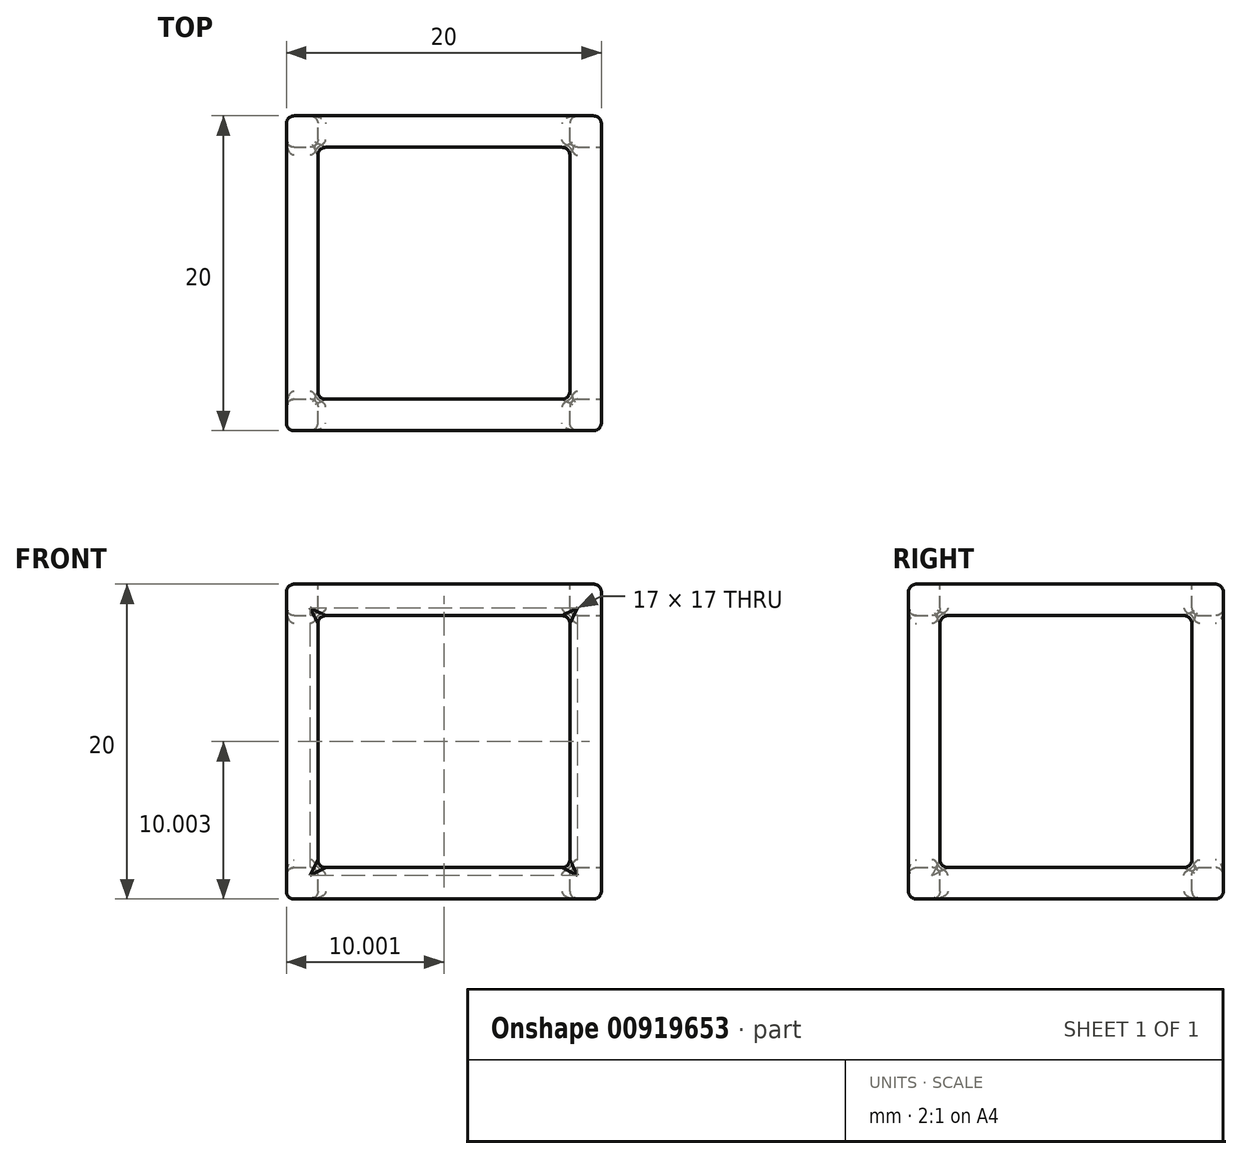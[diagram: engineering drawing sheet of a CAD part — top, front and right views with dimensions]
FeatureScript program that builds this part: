
annotation { "Feature Type Name" : "Feature", "Feature Type Description" : "" }
export const myFeature = defineFeature(function(context is Context, id is Id, definition is map)
    precondition{}
    {
        {
            var Q0;
            Q0=qCreatedBy(makeId("Front.planeOp"),FACE);
            var sketch = newSketch(context, id + "F0", { "sketchPlane" : qUnion([Q0])});
            skLineSegment(sketch, "E0.bottom", {"start": v(-48.8, 17.81) * mm, "end": v(-28.8, 17.81) * mm});
            skLineSegment(sketch, "E0.top", {"start": v(-48.8, -2.19) * mm, "end": v(-28.8, -2.19) * mm});
            skLineSegment(sketch, "E0.left", {"start": v(-48.8, 17.81) * mm, "end": v(-48.8, -2.19) * mm});
            skLineSegment(sketch, "E0.right", {"start": v(-28.8, 17.81) * mm, "end": v(-28.8, -2.23) * mm});
            skLineSegment(sketch, "E1.bottom", {"start": v(-46.8, 15.81) * mm, "end": v(-30.8, 15.81) * mm});
            skLineSegment(sketch, "E1.top", {"start": v(-46.8, -0.19) * mm, "end": v(-30.8, -0.19) * mm});
            skLineSegment(sketch, "E1.left", {"start": v(-46.8, 15.81) * mm, "end": v(-46.8, -0.19) * mm});
            skLineSegment(sketch, "E1.right", {"start": v(-30.8, 15.81) * mm, "end": v(-30.8, -0.19) * mm});
            skPoint(sketch, "E2.visualSharp", {"position": v(-46.8, 15.81) * mm});
            skPoint(sketch, "E3.visualSharp", {"position": v(-48.8, 17.81) * mm});
            skPoint(sketch, "E4.visualSharp", {"position": v(-30.8, 15.81) * mm});
            skPoint(sketch, "E5.visualSharp", {"position": v(-30.8, -0.19) * mm});
            skPoint(sketch, "E6.visualSharp", {"position": v(-46.8, -0.19) * mm});
            skPoint(sketch, "E7.visualSharp", {"position": v(-48.8, -2.19) * mm});
            skPoint(sketch, "E8.visualSharp", {"position": v(-28.8, -2.19) * mm});
            skPoint(sketch, "E9.visualSharp", {"position": v(-28.8, 17.81) * mm});
            skSolve(sketch);
        }
        {
            var Q0;
            Q0 = qSketchRegion(id + "F0", true);
            extrude(context, id + "F1", {"entities" : qUnion([Q0]), "depth" : 20 * mm, "offsetDistance" : 25 * mm});
        }
        {
            var Q0;
            Q0=makeQuery(id+"F1.opExtrude","SWEPT_FACE",FACE,{"disambiguationData":[OSD([sQuery(id+"F0.wireOp",EDGE,"E0.right")])]});
            var sketch = newSketch(context, id + "F2", { "sketchPlane" : qUnion([Q0])});
            skLineSegment(sketch, "E10.bottom", {"start": v(-2, 15.81) * mm, "end": v(-18, 15.81) * mm});
            skLineSegment(sketch, "E10.top", {"start": v(-18, -0.19) * mm, "end": v(-2, -0.19) * mm});
            skLineSegment(sketch, "E10.left", {"start": v(-18, 15.81) * mm, "end": v(-18, -0.19) * mm});
            skLineSegment(sketch, "E10.right", {"start": v(-2, 15.81) * mm, "end": v(-2, -0.19) * mm});
            skSolve(sketch);
        }
        {
            var Q0;
            Q0 = qSketchRegion(id + "F2", true);
            extrude(context, id + "F3", {"entities" : qUnion([Q0]), "operationType" : NewBodyOperationType.REMOVE, "oppositeDirection" : true, "depth" : 25 * mm, "offsetDistance" : 25 * mm});
        }
        {
            var Q0;
            Q0=makeQuery(id+"F1.opExtrude","SWEPT_FACE",FACE,{"disambiguationData":[OSD([sQuery(id+"F0.wireOp",EDGE,"E0.bottom")])]});
            var sketch = newSketch(context, id + "F4", { "sketchPlane" : qUnion([Q0])});
            skLineSegment(sketch, "E11.bottom", {"start": v(-30.8, -18) * mm, "end": v(-46.8, -18) * mm});
            skLineSegment(sketch, "E11.top", {"start": v(-30.8, -2) * mm, "end": v(-46.8, -2) * mm});
            skLineSegment(sketch, "E11.left", {"start": v(-30.8, -18) * mm, "end": v(-30.8, -2) * mm});
            skLineSegment(sketch, "E11.right", {"start": v(-46.8, -18) * mm, "end": v(-46.8, -2) * mm});
            skSolve(sketch);
        }
        {
            var Q0;
            Q0 = qSketchRegion(id + "F4", true);
            extrude(context, id + "F5", {"entities" : qUnion([Q0]), "operationType" : NewBodyOperationType.REMOVE, "oppositeDirection" : true, "depth" : 25 * mm, "offsetDistance" : 25 * mm});
        }
        {
            var Q0;
            Q0=makeQuery(id+"F1.opExtrude","CAP_EDGE",EDGE,{"disambiguationData":[OSD([sQuery(id+"F0.wireOp",EDGE,"E0.bottom")])],"isStart":false});
            var Q1;
            Q1=makeQuery(id+"F1.opExtrude","CAP_EDGE",EDGE,{"disambiguationData":[OSD([sQuery(id+"F0.wireOp",EDGE,"E1.bottom")])],"isStart":false});
            var Q2;
            Q2=makeQuery(id+"F3.boolean.opBoolean","COPY",EDGE,{"derivedFrom":makeQuery(id+"F3.opExtrude","CAP_EDGE",EDGE,{"disambiguationData":[OSD([sQuery(id+"F2.wireOp",EDGE,"E10.left")])],"isStart":true})});
            var Q3;
            Q3=makeQuery(id+"F1.opExtrude","CAP_FACE",FACE,{"disambiguationData":[OSD([sQuery(id+"F0.wireOp",EDGE,"E0.bottom"),sQuery(id+"F0.wireOp",EDGE,"E0.top"),sQuery(id+"F0.wireOp",EDGE,"E0.left"),sQuery(id+"F0.wireOp",EDGE,"E0.right"),sQuery(id+"F0.wireOp",EDGE,"E1.bottom"),sQuery(id+"F0.wireOp",EDGE,"E1.top"),sQuery(id+"F0.wireOp",EDGE,"E1.left"),sQuery(id+"F0.wireOp",EDGE,"E1.right")])],"isStart":false});
            var Q4;
            Q4=makeQuery(id+"F3.boolean.opBoolean","INTERSECT",EDGE,{"derivedFrom":[makeQuery(id+"F1.opExtrude","SWEPT_FACE",FACE,{"disambiguationData":[OSD([sQuery(id+"F0.wireOp",EDGE,"E1.right")])]}),makeQuery(id+"F3.opExtrude","SWEPT_FACE",FACE,{"disambiguationData":[OSD([sQuery(id+"F2.wireOp",EDGE,"E10.left")])]})]});
            var Q5;
            Q5=makeQuery(id+"F3.boolean.opBoolean","INTERSECT",EDGE,{"derivedFrom":[makeQuery(id+"F1.opExtrude","SWEPT_FACE",FACE,{"disambiguationData":[OSD([sQuery(id+"F0.wireOp",EDGE,"E0.left")])]}),makeQuery(id+"F3.opExtrude","SWEPT_FACE",FACE,{"disambiguationData":[OSD([sQuery(id+"F2.wireOp",EDGE,"E10.left")])]})]});
            var Q6;
            Q6=makeQuery(id+"F3.boolean.opBoolean","INTERSECT",EDGE,{"derivedFrom":[makeQuery(id+"F1.opExtrude","SWEPT_FACE",FACE,{"disambiguationData":[OSD([sQuery(id+"F0.wireOp",EDGE,"E0.left")])]}),makeQuery(id+"F3.opExtrude","SWEPT_FACE",FACE,{"disambiguationData":[OSD([sQuery(id+"F2.wireOp",EDGE,"E10.bottom")])]})]});
            var Q7;
            Q7=makeQuery(id+"F5.boolean.opBoolean","INTERSECT",EDGE,{"derivedFrom":[makeQuery(id+"F3.boolean.opBoolean","MERGE",FACE,{"derivedFrom":[makeQuery(id+"F1.opExtrude","SWEPT_FACE",FACE,{"disambiguationData":[OSD([sQuery(id+"F0.wireOp",EDGE,"E1.bottom")])]})],"fromTools":[makeQuery(id+"F3.opExtrude","SWEPT_FACE",FACE,{"disambiguationData":[OSD([sQuery(id+"F2.wireOp",EDGE,"E10.bottom")])]})]}),makeQuery(id+"F5.opExtrude","SWEPT_FACE",FACE,{"disambiguationData":[OSD([sQuery(id+"F4.wireOp",EDGE,"E11.right")])]})]});
            var Q8;
            Q8=makeQuery(id+"F5.boolean.opBoolean","COPY",EDGE,{"derivedFrom":makeQuery(id+"F5.opExtrude","CAP_EDGE",EDGE,{"disambiguationData":[OSD([sQuery(id+"F4.wireOp",EDGE,"E11.right")])],"isStart":true})});
            var Q9;
            Q9=makeQuery(id+"F1.opExtrude","SWEPT_EDGE",EDGE,{"disambiguationData":[OSD([sQuery(id+"F0.wireOp",EDGE,"E0.bottom"),sQuery(id+"F0.wireOp",EDGE,"E0.left")])]});
            var Q10;
            Q10=makeQuery(id+"F3.boolean.opBoolean","INTERSECT",EDGE,{"derivedFrom":[makeQuery(id+"F1.opExtrude","SWEPT_FACE",FACE,{"disambiguationData":[OSD([sQuery(id+"F0.wireOp",EDGE,"E0.left")])]}),makeQuery(id+"F3.opExtrude","SWEPT_FACE",FACE,{"disambiguationData":[OSD([sQuery(id+"F2.wireOp",EDGE,"E10.top")])]})]});
            var Q11;
            Q11=makeQuery(id+"F5.boolean.opBoolean","INTERSECT",EDGE,{"derivedFrom":[makeQuery(id+"F3.boolean.opBoolean","MERGE",FACE,{"derivedFrom":[makeQuery(id+"F1.opExtrude","SWEPT_FACE",FACE,{"disambiguationData":[OSD([sQuery(id+"F0.wireOp",EDGE,"E1.top")])]})],"fromTools":[makeQuery(id+"F3.opExtrude","SWEPT_FACE",FACE,{"disambiguationData":[OSD([sQuery(id+"F2.wireOp",EDGE,"E10.top")])]})]}),makeQuery(id+"F5.opExtrude","SWEPT_FACE",FACE,{"disambiguationData":[OSD([sQuery(id+"F4.wireOp",EDGE,"E11.right")])]})]});
            var Q12;
            Q12=makeQuery(id+"F1.opExtrude","SWEPT_EDGE",EDGE,{"disambiguationData":[OSD([sQuery(id+"F0.wireOp",EDGE,"E0.top"),sQuery(id+"F0.wireOp",EDGE,"E0.left")])]});
            var Q13;
            Q13=makeQuery(id+"F1.opExtrude","CAP_EDGE",EDGE,{"disambiguationData":[OSD([sQuery(id+"F0.wireOp",EDGE,"E0.left")])],"isStart":true});
            var Q14;
            Q14=makeQuery(id+"F3.boolean.opBoolean","INTERSECT",EDGE,{"derivedFrom":[makeQuery(id+"F1.opExtrude","SWEPT_FACE",FACE,{"disambiguationData":[OSD([sQuery(id+"F0.wireOp",EDGE,"E0.left")])]}),makeQuery(id+"F3.opExtrude","SWEPT_FACE",FACE,{"disambiguationData":[OSD([sQuery(id+"F2.wireOp",EDGE,"E10.right")])]})]});
            fillet(context, id + "F6", {"entities" : qUnion([Q0, Q1, Q2, Q3, Q4, Q5, Q6, Q7, Q8, Q9, Q10, Q11, Q12, Q13, Q14]), "radius" : 0.5 * mm, "tangentPropagation" : true, "allowEdgeOverflow" : false});
        }
        {
            var Q0;
            Q0=makeQuery(id+"F5.boolean.opBoolean","INTERSECT",EDGE,{"derivedFrom":[makeQuery(id+"F1.opExtrude","SWEPT_FACE",FACE,{"disambiguationData":[OSD([sQuery(id+"F0.wireOp",EDGE,"E0.top")])]}),makeQuery(id+"F5.opExtrude","SWEPT_FACE",FACE,{"disambiguationData":[OSD([sQuery(id+"F4.wireOp",EDGE,"E11.bottom")])]})]});
            var Q1;
            Q1=makeQuery(id+"F1.opExtrude","SWEPT_EDGE",EDGE,{"disambiguationData":[OSD([sQuery(id+"F0.wireOp",EDGE,"E0.top"),sQuery(id+"F0.wireOp",EDGE,"E0.right")])]});
            var Q2;
            Q2=makeQuery(id+"F5.boolean.opBoolean","INTERSECT",EDGE,{"derivedFrom":[makeQuery(id+"F1.opExtrude","SWEPT_FACE",FACE,{"disambiguationData":[OSD([sQuery(id+"F0.wireOp",EDGE,"E0.top")])]}),makeQuery(id+"F5.opExtrude","SWEPT_FACE",FACE,{"disambiguationData":[OSD([sQuery(id+"F4.wireOp",EDGE,"E11.left")])]})]});
            var Q3;
            Q3=makeQuery(id+"F3.boolean.opBoolean","COPY",EDGE,{"derivedFrom":makeQuery(id+"F3.opExtrude","CAP_EDGE",EDGE,{"disambiguationData":[OSD([sQuery(id+"F2.wireOp",EDGE,"E10.top")])],"isStart":true})});
            var Q4;
            Q4=makeQuery(id+"F5.boolean.opBoolean","INTERSECT",EDGE,{"derivedFrom":[makeQuery(id+"F1.opExtrude","SWEPT_FACE",FACE,{"disambiguationData":[OSD([sQuery(id+"F0.wireOp",EDGE,"E0.top")])]}),makeQuery(id+"F5.opExtrude","SWEPT_FACE",FACE,{"disambiguationData":[OSD([sQuery(id+"F4.wireOp",EDGE,"E11.right")])]})]});
            var Q5;
            Q5=makeQuery(id+"F3.boolean.opBoolean","INTERSECT",EDGE,{"derivedFrom":[makeQuery(id+"F1.opExtrude","SWEPT_FACE",FACE,{"disambiguationData":[OSD([sQuery(id+"F0.wireOp",EDGE,"E1.left")])]}),makeQuery(id+"F3.opExtrude","SWEPT_FACE",FACE,{"disambiguationData":[OSD([sQuery(id+"F2.wireOp",EDGE,"E10.left")])]})]});
            var Q6;
            Q6=makeQuery(id+"F5.boolean.opBoolean","COPY",EDGE,{"derivedFrom":makeQuery(id+"F5.opExtrude","CAP_EDGE",EDGE,{"disambiguationData":[OSD([sQuery(id+"F4.wireOp",EDGE,"E11.bottom")])],"isStart":true})});
            var Q7;
            Q7=makeQuery(id+"F5.boolean.opBoolean","INTERSECT",EDGE,{"derivedFrom":[makeQuery(id+"F3.boolean.opBoolean","MERGE",FACE,{"derivedFrom":[makeQuery(id+"F1.opExtrude","SWEPT_FACE",FACE,{"disambiguationData":[OSD([sQuery(id+"F0.wireOp",EDGE,"E1.bottom")])]})],"fromTools":[makeQuery(id+"F3.opExtrude","SWEPT_FACE",FACE,{"disambiguationData":[OSD([sQuery(id+"F2.wireOp",EDGE,"E10.bottom")])]})]}),makeQuery(id+"F5.opExtrude","SWEPT_FACE",FACE,{"disambiguationData":[OSD([sQuery(id+"F4.wireOp",EDGE,"E11.bottom")])]})]});
            var Q8;
            Q8=makeQuery(id+"F1.opExtrude","SWEPT_EDGE",EDGE,{"disambiguationData":[OSD([sQuery(id+"F0.wireOp",EDGE,"E0.bottom"),sQuery(id+"F0.wireOp",EDGE,"E0.right")])]});
            var Q9;
            Q9=makeQuery(id+"F5.boolean.opBoolean","COPY",EDGE,{"derivedFrom":makeQuery(id+"F5.opExtrude","CAP_EDGE",EDGE,{"disambiguationData":[OSD([sQuery(id+"F4.wireOp",EDGE,"E11.left")])],"isStart":true})});
            var Q10;
            Q10=makeQuery(id+"F3.boolean.opBoolean","COPY",EDGE,{"derivedFrom":makeQuery(id+"F3.opExtrude","CAP_EDGE",EDGE,{"disambiguationData":[OSD([sQuery(id+"F2.wireOp",EDGE,"E10.bottom")])],"isStart":true})});
            var Q11;
            Q11=makeQuery(id+"F3.boolean.opBoolean","COPY",EDGE,{"derivedFrom":makeQuery(id+"F3.opExtrude","CAP_EDGE",EDGE,{"disambiguationData":[OSD([sQuery(id+"F2.wireOp",EDGE,"E10.right")])],"isStart":true})});
            var Q12;
            Q12=makeQuery(id+"F1.opExtrude","CAP_EDGE",EDGE,{"disambiguationData":[OSD([sQuery(id+"F0.wireOp",EDGE,"E0.right")])],"isStart":true});
            var Q13;
            Q13=makeQuery(id+"F1.opExtrude","CAP_EDGE",EDGE,{"disambiguationData":[OSD([sQuery(id+"F0.wireOp",EDGE,"E0.bottom")])],"isStart":true});
            var Q14;
            Q14=makeQuery(id+"F5.boolean.opBoolean","COPY",EDGE,{"derivedFrom":makeQuery(id+"F5.opExtrude","CAP_EDGE",EDGE,{"disambiguationData":[OSD([sQuery(id+"F4.wireOp",EDGE,"E11.top")])],"isStart":true})});
            var Q15;
            Q15=makeQuery(id+"F5.boolean.opBoolean","INTERSECT",EDGE,{"derivedFrom":[makeQuery(id+"F3.boolean.opBoolean","MERGE",FACE,{"derivedFrom":[makeQuery(id+"F1.opExtrude","SWEPT_FACE",FACE,{"disambiguationData":[OSD([sQuery(id+"F0.wireOp",EDGE,"E1.top")])]})],"fromTools":[makeQuery(id+"F3.opExtrude","SWEPT_FACE",FACE,{"disambiguationData":[OSD([sQuery(id+"F2.wireOp",EDGE,"E10.top")])]})]}),makeQuery(id+"F5.opExtrude","SWEPT_FACE",FACE,{"disambiguationData":[OSD([sQuery(id+"F4.wireOp",EDGE,"E11.bottom")])]})]});
            fillet(context, id + "F7", {"entities" : qUnion([Q0, Q1, Q2, Q3, Q4, Q5, Q6, Q7, Q8, Q9, Q10, Q11, Q12, Q13, Q14, Q15]), "radius" : 0.5 * mm, "tangentPropagation" : true, "allowEdgeOverflow" : false});
        }
        {
            var Q0;
            Q0=makeQuery(id+"F3.boolean.opBoolean","INTERSECT",EDGE,{"derivedFrom":[makeQuery(id+"F1.opExtrude","SWEPT_FACE",FACE,{"disambiguationData":[OSD([sQuery(id+"F0.wireOp",EDGE,"E1.left")])]}),makeQuery(id+"F3.opExtrude","SWEPT_FACE",FACE,{"disambiguationData":[OSD([sQuery(id+"F2.wireOp",EDGE,"E10.right")])]})]});
            var Q1;
            Q1=makeQuery(id+"F5.boolean.opBoolean","INTERSECT",EDGE,{"derivedFrom":[makeQuery(id+"F3.boolean.opBoolean","MERGE",FACE,{"derivedFrom":[makeQuery(id+"F1.opExtrude","SWEPT_FACE",FACE,{"disambiguationData":[OSD([sQuery(id+"F0.wireOp",EDGE,"E1.top")])]})],"fromTools":[makeQuery(id+"F3.opExtrude","SWEPT_FACE",FACE,{"disambiguationData":[OSD([sQuery(id+"F2.wireOp",EDGE,"E10.top")])]})]}),makeQuery(id+"F5.opExtrude","SWEPT_FACE",FACE,{"disambiguationData":[OSD([sQuery(id+"F4.wireOp",EDGE,"E11.top")])]})]});
            var Q2;
            Q2=makeQuery(id+"F5.boolean.opBoolean","INTERSECT",EDGE,{"derivedFrom":[makeQuery(id+"F1.opExtrude","SWEPT_FACE",FACE,{"disambiguationData":[OSD([sQuery(id+"F0.wireOp",EDGE,"E0.top")])]}),makeQuery(id+"F5.opExtrude","SWEPT_FACE",FACE,{"disambiguationData":[OSD([sQuery(id+"F4.wireOp",EDGE,"E11.top")])]})]});
            var Q3;
            Q3=makeQuery(id+"F1.opExtrude","CAP_EDGE",EDGE,{"disambiguationData":[OSD([sQuery(id+"F0.wireOp",EDGE,"E1.top")])],"isStart":true});
            var Q4;
            Q4=makeQuery(id+"F1.opExtrude","CAP_EDGE",EDGE,{"disambiguationData":[OSD([sQuery(id+"F0.wireOp",EDGE,"E1.left")])],"isStart":true});
            fillet(context, id + "F8", {"entities" : qUnion([Q0, Q1, Q2, Q3, Q4]), "radius" : 0.5 * mm, "tangentPropagation" : true, "allowEdgeOverflow" : false});
        }
        {
            var Q0;
            Q0=makeQuery(id+"F3.boolean.opBoolean","INTERSECT",EDGE,{"derivedFrom":[makeQuery(id+"F1.opExtrude","SWEPT_FACE",FACE,{"disambiguationData":[OSD([sQuery(id+"F0.wireOp",EDGE,"E1.right")])]}),makeQuery(id+"F3.opExtrude","SWEPT_FACE",FACE,{"disambiguationData":[OSD([sQuery(id+"F2.wireOp",EDGE,"E10.right")])]})]});
            var Q1;
            Q1=makeQuery(id+"F1.opExtrude","CAP_EDGE",EDGE,{"disambiguationData":[OSD([sQuery(id+"F0.wireOp",EDGE,"E1.right")])],"isStart":true});
            var Q2;
            Q2=makeQuery(id+"F5.boolean.opBoolean","INTERSECT",EDGE,{"derivedFrom":[makeQuery(id+"F3.boolean.opBoolean","MERGE",FACE,{"derivedFrom":[makeQuery(id+"F1.opExtrude","SWEPT_FACE",FACE,{"disambiguationData":[OSD([sQuery(id+"F0.wireOp",EDGE,"E1.top")])]})],"fromTools":[makeQuery(id+"F3.opExtrude","SWEPT_FACE",FACE,{"disambiguationData":[OSD([sQuery(id+"F2.wireOp",EDGE,"E10.top")])]})]}),makeQuery(id+"F5.opExtrude","SWEPT_FACE",FACE,{"disambiguationData":[OSD([sQuery(id+"F4.wireOp",EDGE,"E11.left")])]})]});
            fillet(context, id + "F9", {"entities" : qUnion([Q0, Q1, Q2]), "radius" : 0.5 * mm, "tangentPropagation" : true, "allowEdgeOverflow" : false});
        }
        {
            var Q0;
            Q0=makeQuery(id+"F1.opExtrude","CAP_EDGE",EDGE,{"disambiguationData":[OSD([sQuery(id+"F0.wireOp",EDGE,"E0.top")])],"isStart":true});
            var Q1;
            Q1=makeQuery(id+"F5.boolean.opBoolean","INTERSECT",EDGE,{"derivedFrom":[makeQuery(id+"F3.boolean.opBoolean","MERGE",FACE,{"derivedFrom":[makeQuery(id+"F1.opExtrude","SWEPT_FACE",FACE,{"disambiguationData":[OSD([sQuery(id+"F0.wireOp",EDGE,"E1.bottom")])]})],"fromTools":[makeQuery(id+"F3.opExtrude","SWEPT_FACE",FACE,{"disambiguationData":[OSD([sQuery(id+"F2.wireOp",EDGE,"E10.bottom")])]})]}),makeQuery(id+"F5.opExtrude","SWEPT_FACE",FACE,{"disambiguationData":[OSD([sQuery(id+"F4.wireOp",EDGE,"E11.top")])]})]});
            var Q2;
            Q2=makeQuery(id+"F1.opExtrude","CAP_EDGE",EDGE,{"disambiguationData":[OSD([sQuery(id+"F0.wireOp",EDGE,"E1.bottom")])],"isStart":true});
            var Q3;
            Q3=makeQuery(id+"F5.boolean.opBoolean","INTERSECT",EDGE,{"derivedFrom":[makeQuery(id+"F3.boolean.opBoolean","MERGE",FACE,{"derivedFrom":[makeQuery(id+"F1.opExtrude","SWEPT_FACE",FACE,{"disambiguationData":[OSD([sQuery(id+"F0.wireOp",EDGE,"E1.bottom")])]})],"fromTools":[makeQuery(id+"F3.opExtrude","SWEPT_FACE",FACE,{"disambiguationData":[OSD([sQuery(id+"F2.wireOp",EDGE,"E10.bottom")])]})]}),makeQuery(id+"F5.opExtrude","SWEPT_FACE",FACE,{"disambiguationData":[OSD([sQuery(id+"F4.wireOp",EDGE,"E11.left")])]})]});
            var Q4;
            {var subQ0=sQuery(id+"F0.wireOp",EDGE,"E1.left");var subQ1=sQuery(id+"F0.wireOp",EDGE,"E1.bottom");Q4=makeQuery(id+"F3.boolean.opBoolean","SPLIT",EDGE,{"disambiguationData":[TD([makeQuery(id+"F3.opExtrude","SWEPT_FACE",FACE,{"disambiguationData":[OSD([sQuery(id+"F2.wireOp",EDGE,"E10.left")])]})])],"derivedFrom":makeQuery(id+"F1.opExtrude","SWEPT_EDGE",EDGE,{"disambiguationData":[OSD([subQ1,subQ0])]})});}
            var Q5;
            {var subQ2=sQuery(id+"F4.wireOp",EDGE,"E11.bottom");var subQ3=sQuery(id+"F4.wireOp",EDGE,"E11.right");Q5=makeQuery(id+"F5.boolean.opBoolean","COPY",EDGE,{"disambiguationData":[TD([makeQuery(id+"F1.opExtrude","SWEPT_FACE",FACE,{"disambiguationData":[OSD([sQuery(id+"F0.wireOp",EDGE,"E0.bottom")])]})])],"derivedFrom":makeQuery(id+"F5.opExtrude","SWEPT_EDGE",EDGE,{"disambiguationData":[OSD([subQ2,subQ3])]})});}
            var Q6;
            {var subQ0=sQuery(id+"F2.wireOp",EDGE,"E10.bottom");var subQ1=sQuery(id+"F2.wireOp",EDGE,"E10.left");Q6=makeQuery(id+"F3.boolean.opBoolean","COPY",EDGE,{"disambiguationData":[TD([makeQuery(id+"F1.opExtrude","SWEPT_FACE",FACE,{"disambiguationData":[OSD([sQuery(id+"F0.wireOp",EDGE,"E0.left")])]})])],"derivedFrom":makeQuery(id+"F3.opExtrude","SWEPT_EDGE",EDGE,{"disambiguationData":[OSD([subQ0,subQ1])]})});}
            var Q7;
            {var subQ0=sQuery(id+"F2.wireOp",EDGE,"E10.top");var subQ1=sQuery(id+"F2.wireOp",EDGE,"E10.left");Q7=makeQuery(id+"F3.boolean.opBoolean","COPY",EDGE,{"disambiguationData":[TD([makeQuery(id+"F1.opExtrude","SWEPT_FACE",FACE,{"disambiguationData":[OSD([sQuery(id+"F0.wireOp",EDGE,"E0.left")])]})])],"derivedFrom":makeQuery(id+"F3.opExtrude","SWEPT_EDGE",EDGE,{"disambiguationData":[OSD([subQ0,subQ1])]})});}
            var Q8;
            {var subQ0=sQuery(id+"F0.wireOp",EDGE,"E1.left");var subQ1=sQuery(id+"F0.wireOp",EDGE,"E1.top");Q8=makeQuery(id+"F3.boolean.opBoolean","SPLIT",EDGE,{"disambiguationData":[TD([makeQuery(id+"F3.opExtrude","SWEPT_FACE",FACE,{"disambiguationData":[OSD([sQuery(id+"F2.wireOp",EDGE,"E10.left")])]})])],"derivedFrom":makeQuery(id+"F1.opExtrude","SWEPT_EDGE",EDGE,{"disambiguationData":[OSD([subQ1,subQ0])]})});}
            var Q9;
            {var subQ2=sQuery(id+"F4.wireOp",EDGE,"E11.bottom");var subQ3=sQuery(id+"F4.wireOp",EDGE,"E11.right");Q9=makeQuery(id+"F5.boolean.opBoolean","COPY",EDGE,{"disambiguationData":[TD([makeQuery(id+"F1.opExtrude","SWEPT_FACE",FACE,{"disambiguationData":[OSD([sQuery(id+"F0.wireOp",EDGE,"E0.top")])]})])],"derivedFrom":makeQuery(id+"F5.opExtrude","SWEPT_EDGE",EDGE,{"disambiguationData":[OSD([subQ2,subQ3])]})});}
            var Q10;
            {var subQ2=sQuery(id+"F4.wireOp",EDGE,"E11.top");var subQ3=sQuery(id+"F4.wireOp",EDGE,"E11.right");Q10=makeQuery(id+"F5.boolean.opBoolean","COPY",EDGE,{"disambiguationData":[TD([makeQuery(id+"F1.opExtrude","SWEPT_FACE",FACE,{"disambiguationData":[OSD([sQuery(id+"F0.wireOp",EDGE,"E0.top")])]})])],"derivedFrom":makeQuery(id+"F5.opExtrude","SWEPT_EDGE",EDGE,{"disambiguationData":[OSD([subQ2,subQ3])]})});}
            var Q11;
            {var subQ0=sQuery(id+"F2.wireOp",EDGE,"E10.top");var subQ1=sQuery(id+"F2.wireOp",EDGE,"E10.right");Q11=makeQuery(id+"F3.boolean.opBoolean","COPY",EDGE,{"disambiguationData":[TD([makeQuery(id+"F1.opExtrude","SWEPT_FACE",FACE,{"disambiguationData":[OSD([sQuery(id+"F0.wireOp",EDGE,"E0.left")])]})])],"derivedFrom":makeQuery(id+"F3.opExtrude","SWEPT_EDGE",EDGE,{"disambiguationData":[OSD([subQ0,subQ1])]})});}
            var Q12;
            {var subQ0=sQuery(id+"F0.wireOp",EDGE,"E1.left");var subQ1=sQuery(id+"F0.wireOp",EDGE,"E1.top");Q12=makeQuery(id+"F3.boolean.opBoolean","SPLIT",EDGE,{"disambiguationData":[TD([makeQuery(id+"F3.opExtrude","SWEPT_FACE",FACE,{"disambiguationData":[OSD([sQuery(id+"F2.wireOp",EDGE,"E10.right")])]})])],"derivedFrom":makeQuery(id+"F1.opExtrude","SWEPT_EDGE",EDGE,{"disambiguationData":[OSD([subQ1,subQ0])]})});}
            fillet(context, id + "F10", {"entities" : qUnion([Q0, Q1, Q2, Q3, Q4, Q5, Q6, Q7, Q8, Q9, Q10, Q11, Q12]), "radius" : 0.5 * mm, "tangentPropagation" : true, "allowEdgeOverflow" : false});
        }
        {
            var Q0;
            {var subQ0=sQuery(id+"F2.wireOp",EDGE,"E10.bottom");var subQ1=sQuery(id+"F2.wireOp",EDGE,"E10.right");Q0=makeQuery(id+"F3.boolean.opBoolean","COPY",EDGE,{"disambiguationData":[TD([makeQuery(id+"F1.opExtrude","SWEPT_FACE",FACE,{"disambiguationData":[OSD([sQuery(id+"F0.wireOp",EDGE,"E0.left")])]})])],"derivedFrom":makeQuery(id+"F3.opExtrude","SWEPT_EDGE",EDGE,{"disambiguationData":[OSD([subQ0,subQ1])]})});}
            var Q1;
            {var subQ0=sQuery(id+"F0.wireOp",EDGE,"E1.left");var subQ1=sQuery(id+"F0.wireOp",EDGE,"E1.bottom");Q1=makeQuery(id+"F3.boolean.opBoolean","SPLIT",EDGE,{"disambiguationData":[TD([makeQuery(id+"F3.opExtrude","SWEPT_FACE",FACE,{"disambiguationData":[OSD([sQuery(id+"F2.wireOp",EDGE,"E10.right")])]})])],"derivedFrom":makeQuery(id+"F1.opExtrude","SWEPT_EDGE",EDGE,{"disambiguationData":[OSD([subQ1,subQ0])]})});}
            var Q2;
            {var subQ2=sQuery(id+"F4.wireOp",EDGE,"E11.right");var subQ3=sQuery(id+"F4.wireOp",EDGE,"E11.top");Q2=makeQuery(id+"F5.boolean.opBoolean","COPY",EDGE,{"disambiguationData":[TD([makeQuery(id+"F1.opExtrude","SWEPT_FACE",FACE,{"disambiguationData":[OSD([sQuery(id+"F0.wireOp",EDGE,"E0.bottom")])]})])],"derivedFrom":makeQuery(id+"F5.opExtrude","SWEPT_EDGE",EDGE,{"disambiguationData":[OSD([subQ3,subQ2])]})});}
            var Q3;
            {var subQ2=sQuery(id+"F4.wireOp",EDGE,"E11.bottom");var subQ3=sQuery(id+"F4.wireOp",EDGE,"E11.left");Q3=makeQuery(id+"F5.boolean.opBoolean","COPY",EDGE,{"disambiguationData":[TD([makeQuery(id+"F1.opExtrude","SWEPT_FACE",FACE,{"disambiguationData":[OSD([sQuery(id+"F0.wireOp",EDGE,"E0.bottom")])]})])],"derivedFrom":makeQuery(id+"F5.opExtrude","SWEPT_EDGE",EDGE,{"disambiguationData":[OSD([subQ2,subQ3])]})});}
            var Q4;
            {var subQ0=sQuery(id+"F2.wireOp",EDGE,"E10.bottom");var subQ1=sQuery(id+"F2.wireOp",EDGE,"E10.left");Q4=makeQuery(id+"F3.boolean.opBoolean","COPY",EDGE,{"disambiguationData":[TD([makeQuery(id+"F1.opExtrude","SWEPT_FACE",FACE,{"disambiguationData":[OSD([sQuery(id+"F0.wireOp",EDGE,"E0.right")])]})])],"derivedFrom":makeQuery(id+"F3.opExtrude","SWEPT_EDGE",EDGE,{"disambiguationData":[OSD([subQ0,subQ1])]})});}
            var Q5;
            {var subQ0=sQuery(id+"F0.wireOp",EDGE,"E1.right");var subQ1=sQuery(id+"F0.wireOp",EDGE,"E1.bottom");Q5=makeQuery(id+"F3.boolean.opBoolean","SPLIT",EDGE,{"disambiguationData":[TD([makeQuery(id+"F3.opExtrude","SWEPT_FACE",FACE,{"disambiguationData":[OSD([sQuery(id+"F2.wireOp",EDGE,"E10.left")])]})])],"derivedFrom":makeQuery(id+"F1.opExtrude","SWEPT_EDGE",EDGE,{"disambiguationData":[OSD([subQ1,subQ0])]})});}
            var Q6;
            {var subQ2=sQuery(id+"F4.wireOp",EDGE,"E11.bottom");var subQ3=sQuery(id+"F4.wireOp",EDGE,"E11.left");Q6=makeQuery(id+"F5.boolean.opBoolean","COPY",EDGE,{"disambiguationData":[TD([makeQuery(id+"F1.opExtrude","SWEPT_FACE",FACE,{"disambiguationData":[OSD([sQuery(id+"F0.wireOp",EDGE,"E0.top")])]})])],"derivedFrom":makeQuery(id+"F5.opExtrude","SWEPT_EDGE",EDGE,{"disambiguationData":[OSD([subQ2,subQ3])]})});}
            var Q7;
            {var subQ0=sQuery(id+"F0.wireOp",EDGE,"E1.right");var subQ1=sQuery(id+"F0.wireOp",EDGE,"E1.top");Q7=makeQuery(id+"F3.boolean.opBoolean","SPLIT",EDGE,{"disambiguationData":[TD([makeQuery(id+"F3.opExtrude","SWEPT_FACE",FACE,{"disambiguationData":[OSD([sQuery(id+"F2.wireOp",EDGE,"E10.left")])]})])],"derivedFrom":makeQuery(id+"F1.opExtrude","SWEPT_EDGE",EDGE,{"disambiguationData":[OSD([subQ1,subQ0])]})});}
            var Q8;
            {var subQ0=sQuery(id+"F2.wireOp",EDGE,"E10.top");var subQ1=sQuery(id+"F2.wireOp",EDGE,"E10.left");Q8=makeQuery(id+"F3.boolean.opBoolean","COPY",EDGE,{"disambiguationData":[TD([makeQuery(id+"F1.opExtrude","SWEPT_FACE",FACE,{"disambiguationData":[OSD([sQuery(id+"F0.wireOp",EDGE,"E0.right")])]})])],"derivedFrom":makeQuery(id+"F3.opExtrude","SWEPT_EDGE",EDGE,{"disambiguationData":[OSD([subQ0,subQ1])]})});}
            var Q9;
            {var subQ0=sQuery(id+"F2.wireOp",EDGE,"E10.top");var subQ1=sQuery(id+"F2.wireOp",EDGE,"E10.right");Q9=makeQuery(id+"F3.boolean.opBoolean","COPY",EDGE,{"disambiguationData":[TD([makeQuery(id+"F1.opExtrude","SWEPT_FACE",FACE,{"disambiguationData":[OSD([sQuery(id+"F0.wireOp",EDGE,"E0.right")])]})])],"derivedFrom":makeQuery(id+"F3.opExtrude","SWEPT_EDGE",EDGE,{"disambiguationData":[OSD([subQ0,subQ1])]})});}
            var Q10;
            {var subQ0=sQuery(id+"F0.wireOp",EDGE,"E1.right");var subQ1=sQuery(id+"F0.wireOp",EDGE,"E1.top");Q10=makeQuery(id+"F3.boolean.opBoolean","SPLIT",EDGE,{"disambiguationData":[TD([makeQuery(id+"F3.opExtrude","SWEPT_FACE",FACE,{"disambiguationData":[OSD([sQuery(id+"F2.wireOp",EDGE,"E10.right")])]})])],"derivedFrom":makeQuery(id+"F1.opExtrude","SWEPT_EDGE",EDGE,{"disambiguationData":[OSD([subQ1,subQ0])]})});}
            var Q11;
            {var subQ2=sQuery(id+"F4.wireOp",EDGE,"E11.top");var subQ3=sQuery(id+"F4.wireOp",EDGE,"E11.left");Q11=makeQuery(id+"F5.boolean.opBoolean","COPY",EDGE,{"disambiguationData":[TD([makeQuery(id+"F1.opExtrude","SWEPT_FACE",FACE,{"disambiguationData":[OSD([sQuery(id+"F0.wireOp",EDGE,"E0.top")])]})])],"derivedFrom":makeQuery(id+"F5.opExtrude","SWEPT_EDGE",EDGE,{"disambiguationData":[OSD([subQ2,subQ3])]})});}
            var Q12;
            {var subQ0=sQuery(id+"F2.wireOp",EDGE,"E10.bottom");var subQ1=sQuery(id+"F2.wireOp",EDGE,"E10.right");Q12=makeQuery(id+"F3.boolean.opBoolean","COPY",EDGE,{"disambiguationData":[TD([makeQuery(id+"F1.opExtrude","SWEPT_FACE",FACE,{"disambiguationData":[OSD([sQuery(id+"F0.wireOp",EDGE,"E0.right")])]})])],"derivedFrom":makeQuery(id+"F3.opExtrude","SWEPT_EDGE",EDGE,{"disambiguationData":[OSD([subQ0,subQ1])]})});}
            var Q13;
            {var subQ0=sQuery(id+"F0.wireOp",EDGE,"E1.right");var subQ1=sQuery(id+"F0.wireOp",EDGE,"E1.bottom");Q13=makeQuery(id+"F3.boolean.opBoolean","SPLIT",EDGE,{"disambiguationData":[TD([makeQuery(id+"F3.opExtrude","SWEPT_FACE",FACE,{"disambiguationData":[OSD([sQuery(id+"F2.wireOp",EDGE,"E10.right")])]})])],"derivedFrom":makeQuery(id+"F1.opExtrude","SWEPT_EDGE",EDGE,{"disambiguationData":[OSD([subQ1,subQ0])]})});}
            var Q14;
            {var subQ2=sQuery(id+"F4.wireOp",EDGE,"E11.top");var subQ3=sQuery(id+"F4.wireOp",EDGE,"E11.left");Q14=makeQuery(id+"F5.boolean.opBoolean","COPY",EDGE,{"disambiguationData":[TD([makeQuery(id+"F1.opExtrude","SWEPT_FACE",FACE,{"disambiguationData":[OSD([sQuery(id+"F0.wireOp",EDGE,"E0.bottom")])]})])],"derivedFrom":makeQuery(id+"F5.opExtrude","SWEPT_EDGE",EDGE,{"disambiguationData":[OSD([subQ2,subQ3])]})});}
            fillet(context, id + "F11", {"entities" : qUnion([Q0, Q1, Q2, Q3, Q4, Q5, Q6, Q7, Q8, Q9, Q10, Q11, Q12, Q13, Q14]), "radius" : 0.5 * mm, "tangentPropagation" : true, "allowEdgeOverflow" : false});
        }
    });
